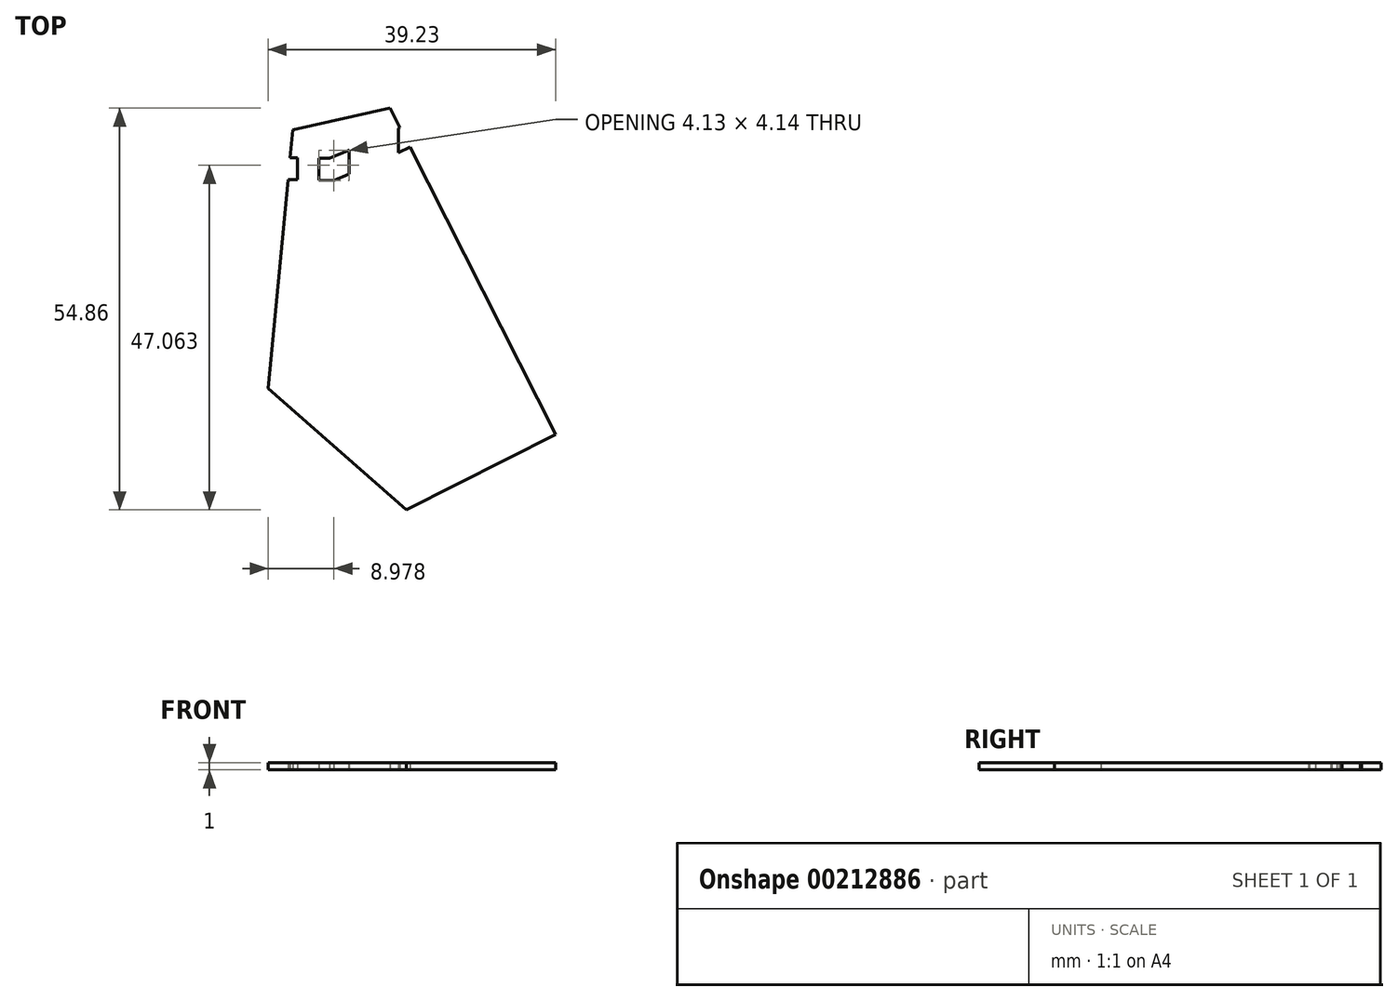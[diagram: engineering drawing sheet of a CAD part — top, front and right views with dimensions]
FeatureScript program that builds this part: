
annotation { "Feature Type Name" : "Feature", "Feature Type Description" : "" }
export const myFeature = defineFeature(function(context is Context, id is Id, definition is map)
    precondition{}
    {
        {
            var Q0;
            Q0=qCreatedBy(makeId("Top.planeOp"),FACE);
            var sketch = newSketch(context, id + "F0", { "sketchPlane" : qUnion([Q0])});
            skLineSegment(sketch, "E0", {"start": v(-10.47, 16.2) * mm, "end": v(-11.95, 16.23) * mm});
            skLineSegment(sketch, "E1", {"start": v(-15.5, 20.08) * mm, "end": v(-2.2, 23.05) * mm});
            skLineSegment(sketch, "E2", {"start": v(-2.2, 23.05) * mm, "end": v(-0.85, 20.4) * mm});
            skLineSegment(sketch, "E3", {"start": v(0.5, 17.71) * mm, "end": v(20.37, -21.5) * mm});
            skLineSegment(sketch, "E4", {"start": v(-9.87, 13.18) * mm, "end": v(-11.95, 13.23) * mm});
            skLineSegment(sketch, "E5.bottom", {"start": v(-7.88, 17.32) * mm, "end": v(-7.82, 17.32) * mm});
            skLineSegment(sketch, "E5.left", {"start": v(-11.95, 16.23) * mm, "end": v(-11.95, 13.23) * mm});
            skLineSegment(sketch, "E5.right", {"start": v(-7.82, 17.32) * mm, "end": v(-7.82, 14.08) * mm});
            skLineSegment(sketch, "E6.right", {"start": v(-14.86, 16.29) * mm, "end": v(-14.86, 13.29) * mm});
            skPoint(sketch, "E7.start.orphan", {"position": v(20.37, -21.5) * mm});
            skLineSegment(sketch, "E8.trimOffspring", {"start": v(-14.86, 16.29) * mm, "end": v(-15.86, 16.3) * mm});
            skLineSegment(sketch, "E9.trimOffspring", {"start": v(-14.86, 13.29) * mm, "end": v(-16.14, 13.31) * mm});
            skLineSegment(sketch, "E10.trimOffspring", {"start": v(-7.82, 14.08) * mm, "end": v(-9.87, 13.18) * mm});
            skLineSegment(sketch, "E11.trimOffspring", {"start": v(-7.88, 17.32) * mm, "end": v(-10.47, 16.2) * mm});
            skLineSegment(sketch, "E12", {"start": v(0, -31.81) * mm, "end": v(20.37, -21.5) * mm});
            skLineSegment(sketch, "E13", {"start": v(-18.86, -15.2) * mm, "end": v(0, -31.81) * mm});
            skLineSegment(sketch, "E14", {"start": v(-18.86, -15.2) * mm, "end": v(-16.14, 13.31) * mm});
            skLineSegment(sketch, "E15", {"start": v(-15.86, 16.3) * mm, "end": v(-15.5, 20.08) * mm});
            skPoint(sketch, "E16.end.orphan", {"position": v(-2.2, 23.05) * mm});
            skLineSegment(sketch, "E17", {"start": v(-1.1, 17.01) * mm, "end": v(0.5, 17.71) * mm});
            skLineSegment(sketch, "E18", {"start": v(-1.1, 20.28) * mm, "end": v(-0.85, 20.4) * mm});
            skLineSegment(sketch, "E19", {"start": v(-1.1, 17.01) * mm, "end": v(-1.1, 20.28) * mm});
            skSolve(sketch);
        }
        {
            var Q0;
            Q0=makeQuery(id+"F0.imprint","IMPRINT",FACE,{"disambiguationData":[TD([[makeQuery(id+"F0.imprint","IMPRINT",EDGE,{"derivedFrom":sQuery(id+"F0.wireOp",EDGE,"E0")}),-1.0]])]});
            extrude(context, id + "F1", {"entities" : qUnion([Q0]), "depth" : 1 * mm});
        }
    });
